# Revit family: FP_Revit_18_RS36A80J1_Fridge_90001167A
name_source: partatom
category: Specialty Equipment
revit_build: Autodesk Revit 2018 (Build: 20170223_1515(x64)
units: mm (PartAtom-declared; Revit-internal decimal feet)

## family parameters
Always vertical = Yes
Cut with Voids When Loaded = Yes
OmniClass Number = 23.40.40.11.11.17
OmniClass Title = Refrigerator-Freezer
Part Type = Normal
Room Calculation Point = No
Round Connector Dimension = Use Diameter
Shared = No
Work Plane-Based = No

## types (3) — shared parameters
Cavity - Depth = 635 mm
Cavity - Width = 914 mm  [stored 2.99869 ft]
Chassis - Depth = 603 mm
Chassis - Height = 1970 mm  [stored 6.46325 ft]
Chassis - Width = 890 mm  [stored 2.91995 ft]
Description = 36" Integrated French Door Refrigerator Freezer, Ice
Handle Style - Contemporary Round (25374 AHS-ASBI-A) = No
Handle Style - Contemporary Square (AHD3RS36A) = No
Handle Style - Contemporary Square Fine (AHD5RD36A) = No
Handle Style - Contemporary Square Fine Black (AHD5RD36AB) = No
Handle Style - Professional Round (AHCRS36A) = No
Handle Style - Professional Square (AHV2RS36A) = No
Manufacturer = Fisher & Paykel Appliances
Material - Body = Fisher & Paykel - Grey
Material - Door Front = Fisher & Paykel - Stainless Steel
Material - Door Structure = Fisher & Paykel - White
Material - Trim = Fisher & Paykel - Stainless Steel
Product - Depth = 621 mm  [stored 2.0374 ft]
Product - Width = 906 mm  [stored 2.97244 ft]
URL = www.fisherpaykel.com
Visibility - Clearance Required = Yes
Visibility - Visibility Control Note = Yes

## per-type parameters (varying)
| type | Cavity - Height | Connector Description - Electrical | Connector Description - Water | Handle Style - Professional Round Flush (AHP3S36A) | Model | Product - Height | Stainless Steel Door Panel Set |
| RS36A80J1 (without door panels) | 2032 mm  [stored 6.66667 ft] | 115 V, 60 Hz, 10 A fused electrical supply | 1/4" (6mm) comp. Stainless steel braided hose | No | RS36A80J1 | 2028 mm  [stored 6.65354 ft] | No |
| RS36A80J1 (with 84" door panel set RD3684A) | 2134 mm  [stored 7.00131 ft] | 115 V, 60 Hz, 10 A, fused electrical supply |  | Yes | RS36A80J1 (with 84" door panel set RD3684A) | 2130 mm  [stored 6.98819 ft] | Yes |
| RS36A80J1 (with 80" door panel set RD3680A) | 2032 mm  [stored 6.66667 ft] | 120 V, 10 A, fused electrical supply | 1/4" (6mm) comp. Stainless steel braided hose | Yes | RS36A80J1 (with 80" door panel set RD3680A) | 2028 mm  [stored 6.65354 ft] | Yes |

note: [stored X ft] marks values corroborated as IEEE doubles in the binary element streams (Revit-internal decimal feet)

## geometry (parser evidence)
native form markers: Sweep x31
no freeform markers — native parametric forms only
